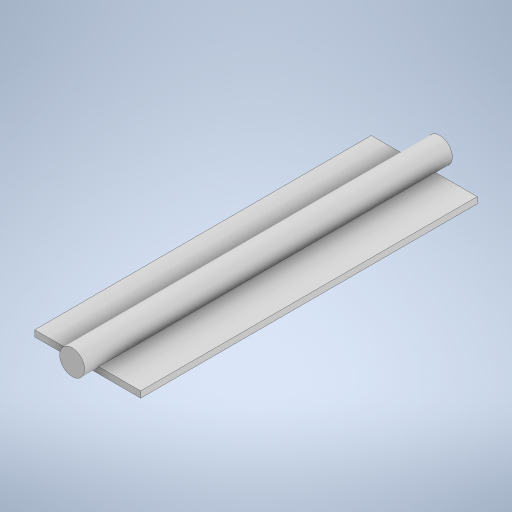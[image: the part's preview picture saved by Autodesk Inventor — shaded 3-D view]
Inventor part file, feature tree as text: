
AUTODESK INVENTOR PART (.ipt)
format: ipt  version: 2024.3 (Build 283343000, 343)  size: 256,000 bytes
history: native  units: mm
features: extrude x2, sketch x2
ambient origin geometry x8: Origin, YZ Plane, XZ Plane, XY Plane, X Axis, Y Axis, Z Axis, Center Point
bodies: Solid1 (feature_tree)
feature tree (4):
  extrude  "Extrusion1"  Depth=108.0mm
  extrude  "Extrusion2"  Depth=118.0mm
  sketch  "Sketch1"  dims[d0=34.0mm d1=108.0mm]
  sketch  "Sketch2"  dims[d2=2.0mm d3=0.0mm d4=8.0mm d5=118.0mm d6=0.0mm]
